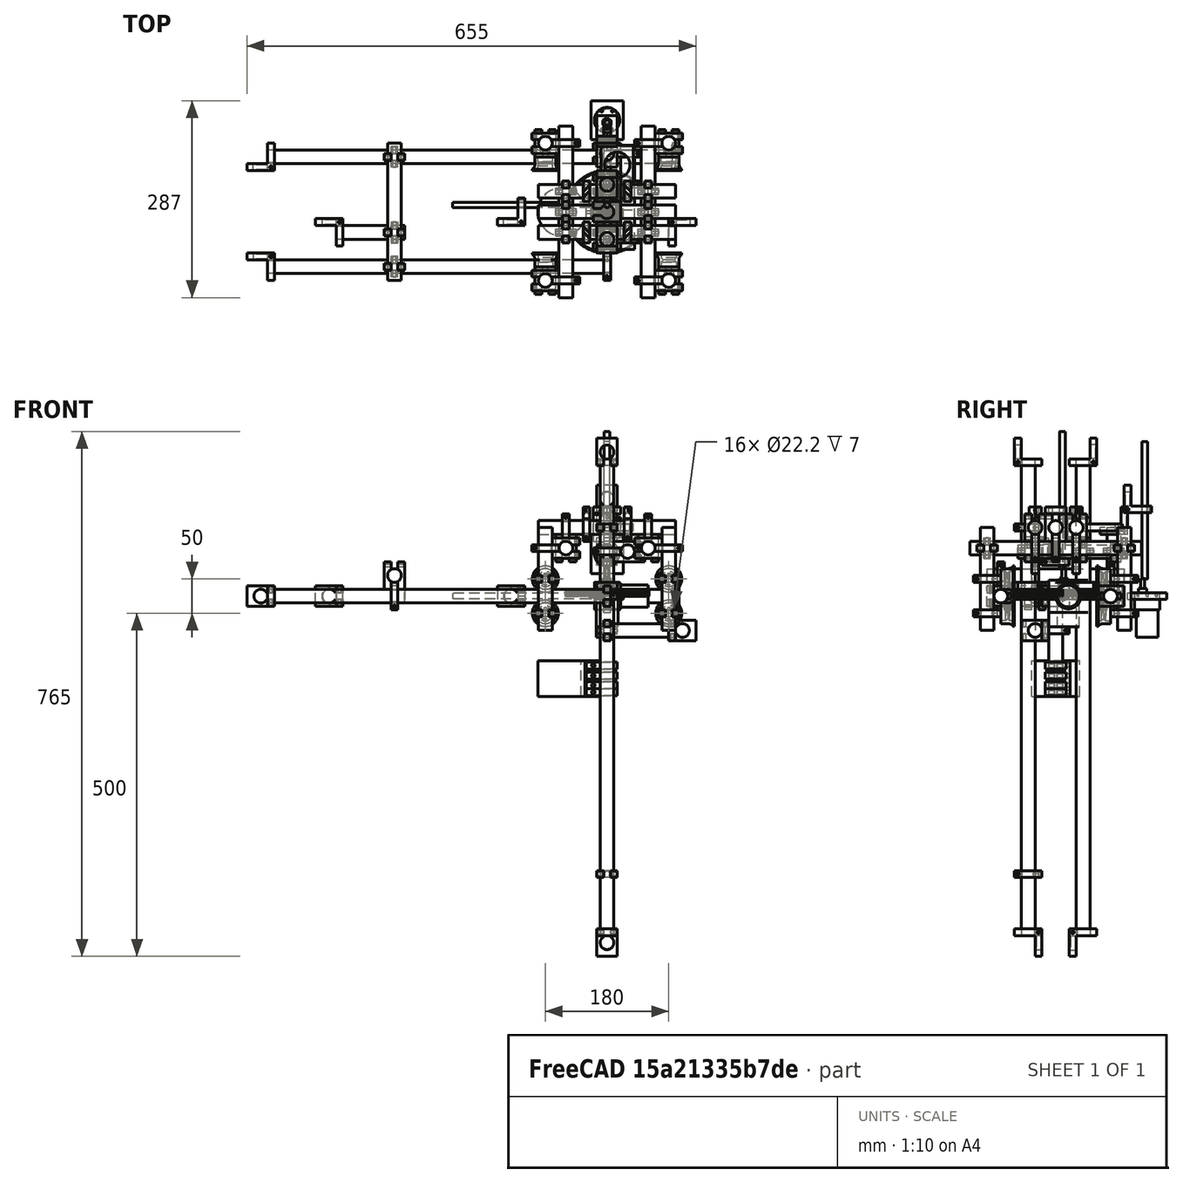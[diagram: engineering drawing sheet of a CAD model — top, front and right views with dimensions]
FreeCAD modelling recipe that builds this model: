
FCSTD DOCUMENT  (FreeCAD 0.17R13522 (Git))
Label: mavis_with_arm
License: All rights reserved
LicenseURL: http://en.wikipedia.org/wiki/All_rights_reserved
objects: Part::FeaturePython×47, Part::Cylinder×16, App::Part×8, App::DocumentObjectGroup×7
note: 63 computed .brp shape members not serialized (recipe doc carries the construction recipe); baked Part::Feature solids carry a one-line shape summary decoded from their .brp

FEATURE [Part::FeaturePython] cogwheel_swivel_01  # a2plus imported part (geometry in sourceFile) (typed FeaturePython)
  fixedPosition = true
  sourceFile = <userpath>/repo/mavis/parts/cogwheel-swivel.fcstd
  timeLastImport = 1.53711e+09
  updateColors = true
FEATURE [Part::Cylinder] Cylinder003
  Angle = 360
  AttacherType = Attacher::AttachEngine3D
  Height = 200
  Placement = pos=(0,-40,0) rot=(0,0,1;0rad)
  Radius = 10
FEATURE [Part::FeaturePython] fastener_l_bearing_003  # a2plus imported part (geometry in sourceFile) (typed FeaturePython)
  Placement = pos=(0,-40,195) rot=(0,0,1;1.5708rad)
  fixedPosition = false
  sourceFile = <userpath>/repo/mavis/parts/fastener-l-bearing.fcstd
  timeLastImport = 1.53709e+09
  updateColors = true
FEATURE [Part::FeaturePython] fastener_join_20mm_01  # a2plus imported part (geometry in sourceFile) (typed FeaturePython)
  Placement = pos=(0,85,65) rot=(0,0,1;0rad)
  fixedPosition = false
  sourceFile = <userpath>/repo/mavis/parts/fastener-join-20mm.fcstd
  timeLastImport = 1.53614e+09
  updateColors = true
FEATURE [Part::FeaturePython] fastener_join_20mm_004  # a2plus imported part (geometry in sourceFile) (typed FeaturePython)
  Placement = pos=(30,-40,65) rot=(0,0.707107,-0.707107;3.14159rad)
  fixedPosition = false
  sourceFile = <userpath>/repo/mavis/parts/fastener-join-20mm.fcstd
  timeLastImport = 1.53614e+09
  updateColors = true
FEATURE [Part::Cylinder] Cylinder007
  Angle = 360
  AttacherType = Attacher::AttachEngine3D
  Height = 200
  Placement = pos=(0,-40,0) rot=(0,0,1;0rad)
  Radius = 10
FEATURE [Part::FeaturePython] fastener_join_20mm_005  # a2plus imported part (geometry in sourceFile) (typed FeaturePython)
  Placement = pos=(30,40,65) rot=(0,0.707107,-0.707107;3.14159rad)
  fixedPosition = false
  sourceFile = <userpath>/repo/mavis/parts/fastener-join-20mm.fcstd
  timeLastImport = 1.53614e+09
  updateColors = true
FEATURE [Part::FeaturePython] fastener_join_20mm_006  # a2plus imported part (geometry in sourceFile) (typed FeaturePython)
  Placement = pos=(0,40,65) rot=(0,0,1;0rad)
  fixedPosition = false
  sourceFile = <userpath>/repo/mavis/parts/fastener-join-20mm.fcstd
  timeLastImport = 1.53614e+09
  updateColors = true
FEATURE [Part::Cylinder] Cylinder008
  Angle = 360
  AttacherType = Attacher::AttachEngine3D
  Height = 200
  Placement = pos=(0,40,0) rot=(0,0,1;0rad)
  Radius = 10
FEATURE [Part::FeaturePython] fastener_l_bearing_005  # a2plus imported part (geometry in sourceFile) (typed FeaturePython)
  Placement = pos=(0,40,195) rot=(0,0,-1;1.5708rad)
  fixedPosition = false
  sourceFile = <userpath>/repo/mavis/parts/fastener-l-bearing.fcstd
  timeLastImport = 1.53709e+09
  updateColors = true
FEATURE [Part::Cylinder] Cylinder010
  Angle = 360
  AttacherType = Attacher::AttachEngine3D
  Height = 150
  Placement = pos=(30,-55,65) rot=(-1,0,0;1.5708rad)
  Radius = 10
FEATURE [Part::FeaturePython] fastener_join_20mm_007  # a2plus imported part (geometry in sourceFile) (typed FeaturePython)
  Placement = pos=(0,-40,65) rot=(0,0,1;0rad)
  fixedPosition = false
  sourceFile = <userpath>/repo/mavis/parts/fastener-join-20mm.fcstd
  timeLastImport = 1.53614e+09
  updateColors = true
FEATURE [Part::FeaturePython] fastener_join_20mm_011  # a2plus imported part (geometry in sourceFile) (typed FeaturePython)
  Placement = pos=(30,85,65) rot=(0,0.707107,-0.707107;3.14159rad)
  fixedPosition = false
  sourceFile = <userpath>/repo/mavis/parts/fastener-join-20mm.fcstd
  timeLastImport = 1.53614e+09
  updateColors = true
FEATURE [Part::Cylinder] Cylinder011
  Angle = 360
  AttacherType = Attacher::AttachEngine3D
  Height = 50
  Placement = pos=(0,85,50) rot=(0,0,1;0rad)
  Radius = 10
FEATURE [Part::FeaturePython] fastener_l_bearing_006  # a2plus imported part (geometry in sourceFile) (typed FeaturePython)
  Placement = pos=(0,85,95) rot=(0,0,-1;1.5708rad)
  fixedPosition = false
  sourceFile = <userpath>/repo/mavis/parts/fastener-l-bearing.fcstd
  timeLastImport = 1.53709e+09
  updateColors = true
FEATURE [App::DocumentObjectGroup] Group001  label="BaseParts"
  Group = -> [fastener_l_bearing_006,fastener_join_20mm_011,Cylinder011,Cylinder003,fastener_join_20mm_007,Cylinder010,fastener_l_bearing_005,Cylinder008,fastener_join_20mm_006,fastener_join_20mm_005,Cylinder007,fastener_join_20mm_004,fastener_join_20mm_01,fastener_l_bearing_003,cogwheel_swivel_01]
FEATURE [Part::Cylinder] Cylinder016
  Angle = 360
  AttacherType = Attacher::AttachEngine3D
  Height = 500
  Placement = pos=(5,-80,0) rot=(0,-1,0;1.5708rad)
  Radius = 10
FEATURE [Part::FeaturePython] fastener_m8_20mm_01003  # a2plus imported part (geometry in sourceFile) (typed FeaturePython)
  Placement = pos=(0,80,0) rot=(0.57735,-0.57735,-0.57735;2.0944rad)
  fixedPosition = false
  sourceFile = <userpath>/repo/mavis/parts/fastener-m8-20mm.fcstd
  timeLastImport = 1.53614e+09
  updateColors = true
FEATURE [Part::FeaturePython] fastener_m8_20mm_01004  # a2plus imported part (geometry in sourceFile) (typed FeaturePython)
  Placement = pos=(100,80,0) rot=(0.57735,0.57735,-0.57735;4.18879rad)
  fixedPosition = false
  sourceFile = <userpath>/repo/mavis/parts/fastener-m8-20mm.fcstd
  timeLastImport = 1.53614e+09
  updateColors = true
FEATURE [Part::FeaturePython] fastener_l_bearing_01005  # a2plus imported part (geometry in sourceFile) (typed FeaturePython)
  Placement = pos=(-390,-30,0) rot=(0.57735,-0.57735,-0.57735;2.0944rad)
  fixedPosition = false
  sourceFile = <userpath>/repo/mavis/parts/fastener-l-bearing.fcstd
  timeLastImport = 1.53709e+09
  updateColors = true
FEATURE [Part::Cylinder] Cylinder017
  Angle = 360
  AttacherType = Attacher::AttachEngine3D
  Height = 100
  Placement = pos=(-295,-30,0) rot=(0,-1,0;1.5708rad)
  Radius = 10
FEATURE [Part::Cylinder] Cylinder018
  Angle = 360
  AttacherType = Attacher::AttachEngine3D
  Height = 200
  Placement = pos=(-310,-100,30) rot=(-1,0,0;1.5708rad)
  Radius = 10
FEATURE [Part::FeaturePython] fastener_join_20mm_015  # a2plus imported part (geometry in sourceFile) (typed FeaturePython)
  Placement = pos=(-310,80,0) rot=(0,-1,0;1.5708rad)
  fixedPosition = false
  sourceFile = <userpath>/repo/mavis/parts/fastener-join-20mm.fcstd
  timeLastImport = 1.53614e+09
  updateColors = true
FEATURE [Part::FeaturePython] fastener_join_20mm_016  # a2plus imported part (geometry in sourceFile) (typed FeaturePython)
  Placement = pos=(-310,80,30) rot=(0.57735,0.57735,-0.57735;2.0944rad)
  fixedPosition = false
  sourceFile = <userpath>/repo/mavis/parts/fastener-join-20mm.fcstd
  timeLastImport = 1.53614e+09
  updateColors = true
FEATURE [Part::FeaturePython] fastener_join_20mm_017  # a2plus imported part (geometry in sourceFile) (typed FeaturePython)
  Placement = pos=(-310,-30,30) rot=(0.57735,0.57735,-0.57735;2.0944rad)
  fixedPosition = false
  sourceFile = <userpath>/repo/mavis/parts/fastener-join-20mm.fcstd
  timeLastImport = 1.53614e+09
  updateColors = true
FEATURE [Part::FeaturePython] fastener_join_20mm_018  # a2plus imported part (geometry in sourceFile) (typed FeaturePython)
  Placement = pos=(-310,-30,0) rot=(0.707107,0,0.707107;3.14159rad)
  fixedPosition = false
  sourceFile = <userpath>/repo/mavis/parts/fastener-join-20mm.fcstd
  timeLastImport = 1.53614e+09
  updateColors = true
FEATURE [Part::FeaturePython] fastener_join_20mm_019  # a2plus imported part (geometry in sourceFile) (typed FeaturePython)
  Placement = pos=(-310,-80,0) rot=(0,-1,0;1.5708rad)
  fixedPosition = false
  sourceFile = <userpath>/repo/mavis/parts/fastener-join-20mm.fcstd
  timeLastImport = 1.53614e+09
  updateColors = true
FEATURE [Part::FeaturePython] fastener_join_20mm_020  # a2plus imported part (geometry in sourceFile) (typed FeaturePython)
  Placement = pos=(-310,-80,30) rot=(0.57735,0.57735,-0.57735;2.0944rad)
  fixedPosition = false
  sourceFile = <userpath>/repo/mavis/parts/fastener-join-20mm.fcstd
  timeLastImport = 1.53614e+09
  updateColors = true
FEATURE [Part::FeaturePython] fastener_m8_20mm_01005  # a2plus imported part (geometry in sourceFile) (typed FeaturePython)
  Placement = pos=(0,-80,0) rot=(0.57735,0.57735,-0.57735;4.18879rad)
  fixedPosition = false
  sourceFile = <userpath>/repo/mavis/parts/fastener-m8-20mm.fcstd
  timeLastImport = 1.53614e+09
  updateColors = true
FEATURE [Part::FeaturePython] fastener_l_bearing_01006  # a2plus imported part (geometry in sourceFile) (typed FeaturePython)
  Placement = pos=(-490,80,0) rot=(0.57735,0.57735,-0.57735;4.18879rad)
  fixedPosition = false
  sourceFile = <userpath>/repo/mavis/parts/fastener-l-bearing.fcstd
  timeLastImport = 1.53709e+09
  updateColors = true
FEATURE [Part::FeaturePython] fastener_l_bearing_01007  # a2plus imported part (geometry in sourceFile) (typed FeaturePython)
  Placement = pos=(-490,-80,0) rot=(0.57735,-0.57735,-0.57735;2.0944rad)
  fixedPosition = false
  sourceFile = <userpath>/repo/mavis/parts/fastener-l-bearing.fcstd
  timeLastImport = 1.53709e+09
  updateColors = true
FEATURE [Part::Cylinder] Cylinder019
  Angle = 360
  AttacherType = Attacher::AttachEngine3D
  Height = 600
  Placement = pos=(105,80,0) rot=(0,-1,0;1.5708rad)
  Radius = 10
FEATURE [App::DocumentObjectGroup] Group002  label="ArmParts"
  Group = -> [Cylinder016,fastener_m8_20mm_01003,fastener_m8_20mm_01004,fastener_l_bearing_01005,Cylinder017,Cylinder018,fastener_join_20mm_015,fastener_join_20mm_016,fastener_join_20mm_017,fastener_join_20mm_018,fastener_join_20mm_019,fastener_join_20mm_020,fastener_m8_20mm_01005,fastener_l_bearing_01006,fastener_l_bearing_01007,Cylinder019]
FEATURE [Part::Cylinder] Cylinder020
  Angle = 360
  AttacherType = Attacher::AttachEngine3D
  Height = 500
  Placement = pos=(0,40,5) rot=(0,1,0;3.14159rad)
  Radius = 10
FEATURE [Part::FeaturePython] fastener_m8_20mm_01006  # a2plus imported part (geometry in sourceFile) (typed FeaturePython)
  Placement = pos=(0,-40,100) rot=(0,0,1;1.5708rad)
  fixedPosition = false
  sourceFile = <userpath>/repo/mavis/parts/fastener-m8-20mm.fcstd
  timeLastImport = 1.53614e+09
  updateColors = true
FEATURE [Part::FeaturePython] fastener_m8_20mm_01007  # a2plus imported part (geometry in sourceFile) (typed FeaturePython)
  Placement = pos=(0,-40,0) rot=(0,0,-1;1.5708rad)
  fixedPosition = false
  sourceFile = <userpath>/repo/mavis/parts/fastener-m8-20mm.fcstd
  timeLastImport = 1.53614e+09
  updateColors = true
FEATURE [Part::FeaturePython] fastener_m8_20mm_01008  # a2plus imported part (geometry in sourceFile) (typed FeaturePython)
  Placement = pos=(0,40,0) rot=(0,0,1;1.5708rad)
  fixedPosition = false
  sourceFile = <userpath>/repo/mavis/parts/fastener-m8-20mm.fcstd
  timeLastImport = 1.53614e+09
  updateColors = true
FEATURE [Part::Cylinder] Cylinder021
  Angle = 360
  AttacherType = Attacher::AttachEngine3D
  Height = 600
  Placement = pos=(0,-40,105) rot=(0,1,0;3.14159rad)
  Radius = 10
FEATURE [Part::FeaturePython] fastener_l_bearing_01008  # a2plus imported part (geometry in sourceFile) (typed FeaturePython)
  Placement = pos=(0,40,-490) rot=(0.707107,0.707107,0;3.14159rad)
  fixedPosition = false
  sourceFile = <userpath>/repo/mavis/parts/fastener-l-bearing.fcstd
  timeLastImport = 1.53709e+09
  updateColors = true
FEATURE [Part::FeaturePython] fastener_l_bearing_01009  # a2plus imported part (geometry in sourceFile) (typed FeaturePython)
  Placement = pos=(0,-40,-490) rot=(0.707107,-0.707107,0;3.14159rad)
  fixedPosition = false
  sourceFile = <userpath>/repo/mavis/parts/fastener-l-bearing.fcstd
  timeLastImport = 1.53709e+09
  updateColors = true
FEATURE [Part::FeaturePython] fastener_m8_20mm_01009  # a2plus imported part (geometry in sourceFile) (typed FeaturePython)
  Placement = pos=(0,-40,-405) rot=(0,0,1;1.5708rad)
  fixedPosition = false
  sourceFile = <userpath>/repo/mavis/parts/fastener-m8-20mm.fcstd
  timeLastImport = 1.53614e+09
  updateColors = true
FEATURE [App::DocumentObjectGroup] Group003  label="LowerArmParts"
  Group = -> [Cylinder020,fastener_m8_20mm_01006,fastener_m8_20mm_01007,fastener_m8_20mm_01008,Cylinder021,fastener_l_bearing_01008,fastener_l_bearing_01009,fastener_m8_20mm_01009]
FEATURE [Part::Cylinder] Cylinder022
  Angle = 360
  AttacherType = Attacher::AttachEngine3D
  Height = 150
  Placement = pos=(0,0,-145) rot=(0,0,1;0rad)
  Radius = 10
FEATURE [Part::FeaturePython] fastener_join_20mm_021  # a2plus imported part (geometry in sourceFile) (typed FeaturePython)
  Placement = pos=(0,-30,-50) rot=(0.57735,0.57735,0.57735;2.0944rad)
  fixedPosition = false
  sourceFile = <userpath>/repo/mavis/parts/fastener-join-20mm.fcstd
  timeLastImport = 1.53614e+09
  updateColors = true
FEATURE [Part::FeaturePython] fastener_join_20mm_022  # a2plus imported part (geometry in sourceFile) (typed FeaturePython)
  Placement = pos=(0,0,-50) rot=(0,0,-1;1.5708rad)
  fixedPosition = false
  sourceFile = <userpath>/repo/mavis/parts/fastener-join-20mm.fcstd
  timeLastImport = 1.53614e+09
  updateColors = true
FEATURE [Part::Cylinder] Cylinder023
  Angle = 360
  AttacherType = Attacher::AttachEngine3D
  Height = 110
  Placement = pos=(-10,-30,-50) rot=(0,1,0;1.5708rad)
  Radius = 10
FEATURE [Part::FeaturePython] fastener_l_bearing_01010  # a2plus imported part (geometry in sourceFile) (typed FeaturePython)
  Placement = pos=(95,-30,-50) rot=(0.57735,-0.57735,0.57735;4.18879rad)
  fixedPosition = true
  sourceFile = <userpath>/repo/mavis/parts/fastener-l-bearing.fcstd
  timeLastImport = 1.53709e+09
  updateColors = true
FEATURE [Part::FeaturePython] fastener_m8_double_002  # a2plus imported part (geometry in sourceFile) (typed FeaturePython)
  Placement = pos=(0,0,0) rot=(0,0,1;1.5708rad)
  fixedPosition = false
  sourceFile = <userpath>/repo/mavis/parts/fastener-m8-double.fcstd
  timeLastImport = 1.53754e+09
  updateColors = true
FEATURE [Part::FeaturePython] utm_mount_005  # a2plus imported part (geometry in sourceFile) (typed FeaturePython)
  Placement = pos=(0,0,-140) rot=(0,0,1;0rad)
  fixedPosition = false
  sourceFile = <userpath>/repo/mavis/parts/utm-mount.fcstd
  timeLastImport = 1.53754e+09
  updateColors = true
FEATURE [Part::FeaturePython] utm_mount_006  # a2plus imported part (geometry in sourceFile) (typed FeaturePython)
  Placement = pos=(0,0,-101) rot=(0,0,1;0rad)
  fixedPosition = false
  sourceFile = <userpath>/repo/mavis/parts/utm-mount.fcstd
  timeLastImport = 1.53754e+09
  updateColors = true
FEATURE [Part::FeaturePython] utm_mount_007  # a2plus imported part (geometry in sourceFile) (typed FeaturePython)
  Placement = pos=(0,0,-116) rot=(0,0,1;0rad)
  fixedPosition = false
  sourceFile = <userpath>/repo/mavis/parts/utm-mount.fcstd
  timeLastImport = 1.53754e+09
  updateColors = true
FEATURE [Part::FeaturePython] utm_mount_008  # a2plus imported part (geometry in sourceFile) (typed FeaturePython)
  Placement = pos=(0,0,-130) rot=(0,0,1;0rad)
  fixedPosition = false
  sourceFile = <userpath>/repo/mavis/parts/utm-mount.fcstd
  timeLastImport = 1.53754e+09
  updateColors = true
FEATURE [Part::FeaturePython] DC_Gear_Motor_37mm_004  # a2plus imported part (geometry in sourceFile) (typed FeaturePython)
  Placement = pos=(0,133.5,-60) rot=(0,0,-1;1.5708rad)
  fixedPosition = false
  sourceFile = <userpath>/.FreeCAD/Mod/parts_library/Electrical Parts/Motors/DC_Gear_Motor_37mm.fcstd
  timeLastImport = 1.53685e+09
  updateColors = true
FEATURE [Part::FeaturePython] fastener_l_bearing_nut_004  # a2plus imported part (geometry in sourceFile) (typed FeaturePython)
  Placement = pos=(0,120,141.4) rot=(0,0,1;1.5708rad)
  fixedPosition = false
  sourceFile = <userpath>/repo/mavis/parts/fastener-l-bearing-nut.fcstd
  timeLastImport = 1.53675e+09
  updateColors = true
FEATURE [Part::FeaturePython] fastener_join_37mm_005  # a2plus imported part (geometry in sourceFile) (typed FeaturePython)
  Placement = pos=(0,115,0) rot=(0,0,1;1.5708rad)
  fixedPosition = false
  sourceFile = <userpath>/repo/mavis/parts/fastener-join-37mm.fcstd
  timeLastImport = 1.53614e+09
  updateColors = true
FEATURE [Part::Cylinder] Cylinder024
  Angle = 360
  AttacherType = Attacher::AttachEngine3D
  Height = 200
  Placement = pos=(0,130,25) rot=(0,0,1;0rad)
  Radius = 4
FEATURE [App::DocumentObjectGroup] Group005  label="ArmSwivelParts"
  Group = -> [DC_Gear_Motor_37mm_004,fastener_l_bearing_nut_004,fastener_join_37mm_005,Cylinder024]
FEATURE [App::Part] Part003  label="ArmSwivel"
  Group = -> [Group005,DC_Gear_Motor_37mm_004,fastener_l_bearing_nut_004,fastener_join_37mm_005,Cylinder024]
  License = CC BY 3.0
  LicenseURL = http://creativecommons.org/licenses/by/3.0/
  Origin = -> Origin009
  Placement = pos=(0,0,110) rot=(0,-1,0;5.49779rad)
FEATURE [Part::FeaturePython] fastener_join_37mm_006  # a2plus imported part (geometry in sourceFile) (typed FeaturePython)
  Placement = pos=(0,0,0) rot=(0.57735,0.57735,0.57735;2.0944rad)
  fixedPosition = false
  sourceFile = <userpath>/repo/mavis/parts/fastener-join-37mm.fcstd
  timeLastImport = 1.53614e+09
  updateColors = true
FEATURE [Part::FeaturePython] DC_Gear_Motor_37mm_005  # a2plus imported part (geometry in sourceFile) (typed FeaturePython)
  Placement = pos=(60,18.5,0) rot=(0.57735,-0.57735,-0.57735;2.0944rad)
  fixedPosition = false
  sourceFile = <userpath>/.FreeCAD/Mod/parts_library/Electrical Parts/Motors/DC_Gear_Motor_37mm.fcstd
  timeLastImport = 1.53685e+09
  updateColors = true
FEATURE [Part::FeaturePython] fastener_l_bearing_nut_005  # a2plus imported part (geometry in sourceFile) (typed FeaturePython)
  Placement = pos=(-140,0,0) rot=(0.57735,0.57735,-0.57735;4.18879rad)
  fixedPosition = false
  sourceFile = <userpath>/repo/mavis/parts/fastener-l-bearing-nut.fcstd
  timeLastImport = 1.53675e+09
  updateColors = true
FEATURE [Part::Cylinder] Cylinder025
  Angle = 360
  AttacherType = Attacher::AttachEngine3D
  Height = 200
  Placement = pos=(-25,10,0) rot=(0,-1,0;1.5708rad)
  Radius = 4
FEATURE [App::DocumentObjectGroup] Group006  label="LowerArmSwivelParts"
  Group = -> [fastener_join_37mm_006,DC_Gear_Motor_37mm_005,fastener_l_bearing_nut_005,Cylinder025]
FEATURE [App::Part] Part004  label="LowerArmSwivel"
  Group = -> [DC_Gear_Motor_37mm_005,fastener_l_bearing_nut_005,fastener_join_37mm_006,Group006,Cylinder025]
  License = CC BY 3.0
  LicenseURL = http://creativecommons.org/licenses/by/3.0/
  Origin = -> Origin010
  Placement = pos=(-405,0,0) rot=(0,1,0;0.785398rad)
FEATURE [Part::FeaturePython] fastener_join_37mm_007  # a2plus imported part (geometry in sourceFile) (typed FeaturePython)
  Placement = pos=(0,0,0) rot=(0,0,1;1.5708rad)
  fixedPosition = false
  sourceFile = <userpath>/repo/mavis/parts/fastener-join-37mm.fcstd
  timeLastImport = 1.53614e+09
  updateColors = true
FEATURE [Part::FeaturePython] fastener_l_bearing_nut_006  # a2plus imported part (geometry in sourceFile) (typed FeaturePython)
  Placement = pos=(0,0,65) rot=(0,0,1;1.5708rad)
  fixedPosition = false
  sourceFile = <userpath>/repo/mavis/parts/fastener-l-bearing-nut.fcstd
  timeLastImport = 1.53675e+09
  updateColors = true
FEATURE [Part::FeaturePython] DC_Gear_Motor_37mm_006  # a2plus imported part (geometry in sourceFile) (typed FeaturePython)
  Placement = pos=(0,18.5,-45) rot=(0,0,-1;1.5708rad)
  fixedPosition = false
  sourceFile = <userpath>/.FreeCAD/Mod/parts_library/Electrical Parts/Motors/DC_Gear_Motor_37mm.fcstd
  timeLastImport = 1.53685e+09
  updateColors = true
FEATURE [Part::Cylinder] Cylinder026
  Angle = 360
  AttacherType = Attacher::AttachEngine3D
  Height = 200
  Placement = pos=(0,10,40) rot=(0,0,1;0rad)
  Radius = 4
FEATURE [App::DocumentObjectGroup] Group007  label="TipSwivelParts"
  Group = -> [fastener_join_37mm_007,fastener_l_bearing_nut_006,DC_Gear_Motor_37mm_006,Cylinder026]
FEATURE [App::Part] Part005  label="TipSwivel"
  Group = -> [fastener_l_bearing_nut_006,Cylinder026,DC_Gear_Motor_37mm_006,fastener_join_37mm_007,Group007]
  License = CC BY 3.0
  LicenseURL = http://creativecommons.org/licenses/by/3.0/
  Origin = -> Origin011
  Placement = pos=(110,0,-50) rot=(0,1,0;6.02139rad)
FEATURE [Part::FeaturePython] utm_mock_01  # a2plus imported part (geometry in sourceFile) (typed FeaturePython)
  Placement = pos=(-66,0,-146) rot=(0,0,1;0rad)
  fixedPosition = false
  sourceFile = <userpath>/repo/mavis/assemblies/utm-mock.fcstd
  timeLastImport = 1.53769e+09
  updateColors = true
FEATURE [App::DocumentObjectGroup] Group004  label="TipParts"
  Group = -> [Cylinder022,fastener_join_20mm_021,fastener_join_20mm_022,Cylinder023,fastener_l_bearing_01010,fastener_m8_double_002,utm_mount_005,utm_mount_006,utm_mount_007,utm_mount_008,utm_mock_01]
FEATURE [App::Part] Part002  label="Tip"
  Group = -> [utm_mount_008,utm_mount_007,Cylinder022,Cylinder023,fastener_join_20mm_021,fastener_join_20mm_022,utm_mount_006,utm_mount_005,fastener_l_bearing_01010,fastener_m8_double_002,Group004,Part005,utm_mock_01]
  License = CC BY 3.0
  LicenseURL = http://creativecommons.org/licenses/by/3.0/
  Origin = -> Origin008
  Placement = pos=(0,0,-505) rot=(0,-1,0;0.261799rad)
FEATURE [App::Part] Part001  label="LowerArm"
  Group = -> [Group003,Cylinder020,fastener_m8_20mm_01006,fastener_m8_20mm_01007,fastener_m8_20mm_01008,Cylinder021,fastener_l_bearing_01008,fastener_l_bearing_01009,fastener_m8_20mm_01009,Part002]
  License = CC BY 3.0
  LicenseURL = http://creativecommons.org/licenses/by/3.0/
  Origin = -> Origin007
  Placement = pos=(-505,0,0) rot=(0,1,0;6.02139rad)
FEATURE [App::Part] Part  label="Arm"
  Group = -> [Group002,Cylinder016,fastener_m8_20mm_01003,fastener_m8_20mm_01004,fastener_l_bearing_01005,Cylinder017,Cylinder018,fastener_join_20mm_015,fastener_join_20mm_016,fastener_join_20mm_017,fastener_join_20mm_018,fastener_join_20mm_019,fastener_join_20mm_020,fastener_m8_20mm_01005,fastener_l_bearing_01006,fastener_l_bearing_01007,Cylinder019,Part001,Part004]
  License = CC BY 3.0
  LicenseURL = http://creativecommons.org/licenses/by/3.0/
  Origin = -> Origin006
  Placement = pos=(0,0,210) rot=(0,1,0;0.523599rad)
FEATURE [Part::FeaturePython] mavis_01  # a2plus imported part (geometry in sourceFile) (typed FeaturePython)
  fixedPosition = false
  sourceFile = <userpath>/repo/mavis/assemblies/mavis.fcstd
  timeLastImport = 1.53769e+09
  updateColors = true
FEATURE [App::Part] Part006  label="ArmAssembly"
  Group = -> [Cylinder011,fastener_join_20mm_004,fastener_join_20mm_01,Cylinder003,fastener_join_20mm_011,fastener_l_bearing_003,fastener_join_20mm_006,Cylinder008,Cylinder007,fastener_join_20mm_007,fastener_join_20mm_005,fastener_l_bearing_006,fastener_l_bearing_005,Cylinder010,cogwheel_swivel_01,Group001,Part,Part003]
  License = CC BY 3.0
  LicenseURL = http://creativecommons.org/licenses/by/3.0/
  Origin = -> Origin
  Placement = pos=(0,0,136) rot=(0,0,1;1.5708rad)
FEATURE [App::Part] Part007  label="MavisWithArm"
  Group = -> [mavis_01,Part006]
  License = CC BY 3.0
  LicenseURL = http://creativecommons.org/licenses/by/3.0/
  Origin = -> Origin012
